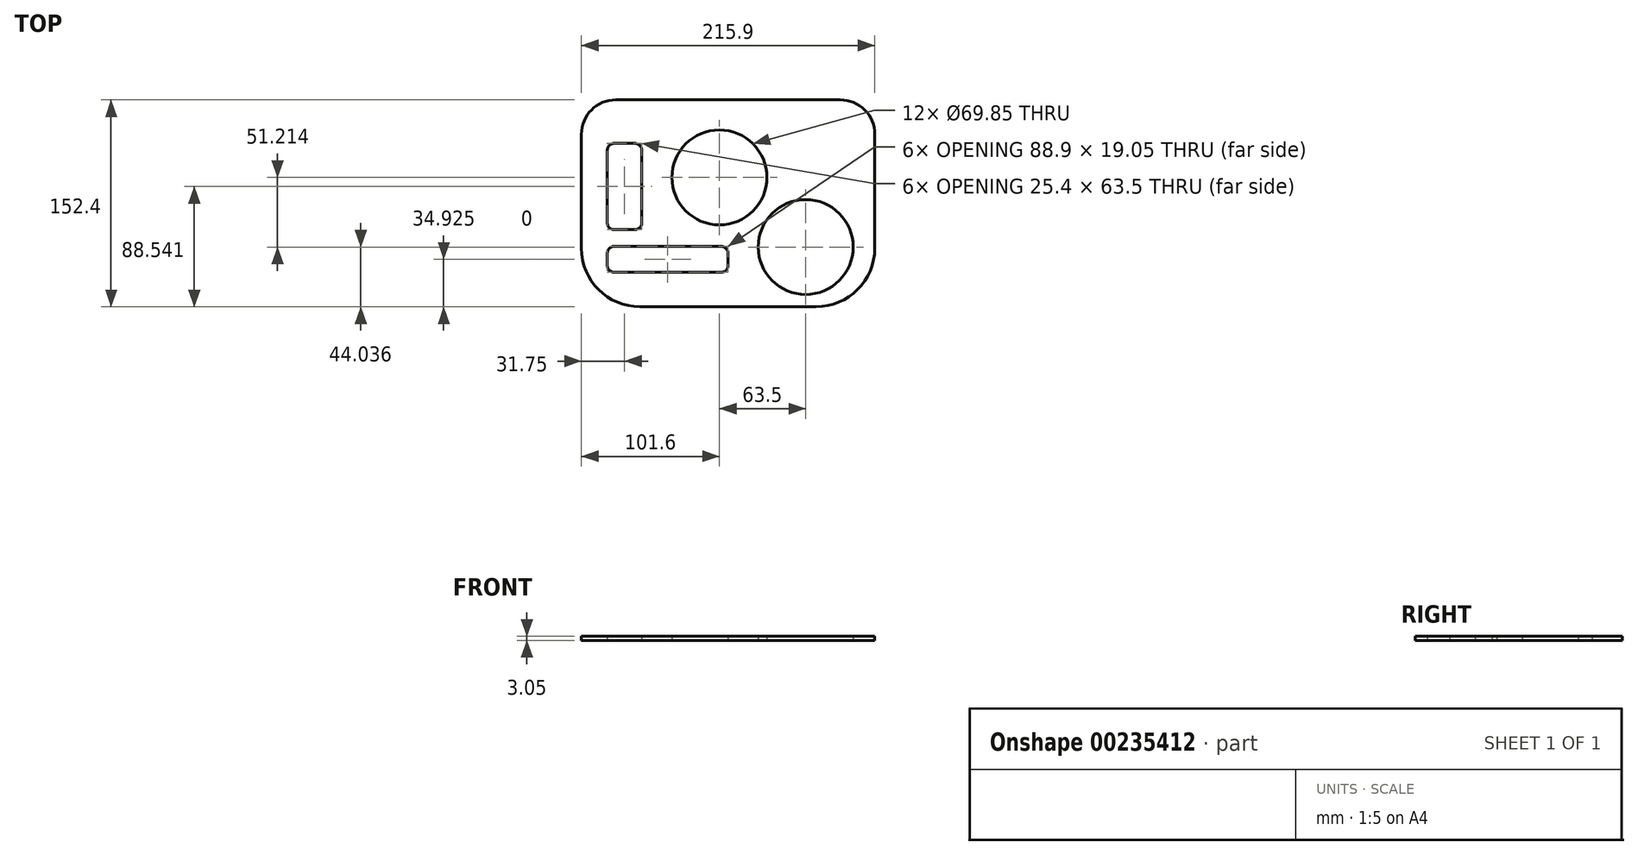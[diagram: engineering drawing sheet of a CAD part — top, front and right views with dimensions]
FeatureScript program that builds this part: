
annotation { "Feature Type Name" : "Feature", "Feature Type Description" : "" }
export const myFeature = defineFeature(function(context is Context, id is Id, definition is map)
    precondition{}
    {
        {
            var Q0;
            Q0=qCreatedBy(makeId("Top.planeOp"),FACE);
            var sketch = newSketch(context, id + "F0", { "sketchPlane" : qUnion([Q0])});
            skLineSegment(sketch, "E0.bottom", {"start": v(107.95, 76.2) * mm, "end": v(-107.95, 76.2) * mm});
            skLineSegment(sketch, "E0.top", {"start": v(107.95, -76.2) * mm, "end": v(-107.95, -76.2) * mm});
            skLineSegment(sketch, "E0.left", {"start": v(107.95, 76.2) * mm, "end": v(107.95, -76.2) * mm});
            skLineSegment(sketch, "E0.right", {"start": v(-107.95, 76.2) * mm, "end": v(-107.95, -76.2) * mm});
            skPoint(sketch, "E0.middle", {"position": v(0, 0) * mm});
            skSolve(sketch);
        }
        {
            var Q0;
            Q0 = qSketchRegion(id + "F0", true);
            extrude(context, id + "F1", {"entities" : qUnion([Q0]), "depth" : 3.05 * mm});
        }
        {
            var Q0;
            Q0=qCreatedBy(makeId("Top.planeOp"),FACE);
            var sketch = newSketch(context, id + "F2", { "sketchPlane" : qUnion([Q0])});
            skLineSegment(sketch, "E1.bottom", {"start": v(-63.5, -19.4) * mm, "end": v(-88.9, -19.4) * mm});
            skLineSegment(sketch, "E1.top", {"start": v(-63.5, 44.1) * mm, "end": v(-88.9, 44.1) * mm});
            skLineSegment(sketch, "E1.left", {"start": v(-63.5, -19.4) * mm, "end": v(-63.5, 44.1) * mm});
            skLineSegment(sketch, "E1.right", {"start": v(-88.9, -19.4) * mm, "end": v(-88.9, 44.1) * mm});
            skPoint(sketch, "E1.middle", {"position": v(-76.2, 12.34) * mm});
            skCircle(sketch, "E2", {"center": v(-6.35, 19.05) * mm, "radius": 34.93 * mm});
            skCircle(sketch, "E3", {"center": v(57.15, -32.16) * mm, "radius": 34.93 * mm});
            skLineSegment(sketch, "E4.bottom", {"start": v(0, -50.8) * mm, "end": v(-88.9, -50.8) * mm});
            skLineSegment(sketch, "E4.top", {"start": v(0, -31.75) * mm, "end": v(-88.9, -31.75) * mm});
            skLineSegment(sketch, "E4.left", {"start": v(0, -50.8) * mm, "end": v(0, -31.75) * mm});
            skLineSegment(sketch, "E4.right", {"start": v(-88.9, -50.8) * mm, "end": v(-88.9, -31.75) * mm});
            skPoint(sketch, "E4.middle", {"position": v(-44.45, -41.27) * mm});
            skSolve(sketch);
        }
        {
            var Q0;
            Q0 = qSketchRegion(id + "F2", true);
            extrude(context, id + "F3", {"entities" : qUnion([Q0]), "operationType" : NewBodyOperationType.REMOVE, "depth" : 25.4 * mm});
        }
        {
            var Q0;
            Q0=makeQuery(id+"F1.opExtrude","SWEPT_EDGE",EDGE,{"disambiguationData":[OSD([sQuery(id+"F0.wireOp",EDGE,"E0.top"),sQuery(id+"F0.wireOp",EDGE,"E0.right")])]});
            var Q1;
            Q1=makeQuery(id+"F1.opExtrude","SWEPT_EDGE",EDGE,{"disambiguationData":[OSD([sQuery(id+"F0.wireOp",EDGE,"E0.top"),sQuery(id+"F0.wireOp",EDGE,"E0.left")])]});
            fillet(context, id + "F4", {"entities" : qUnion([Q0, Q1]), "radius" : 43.18 * mm, "tangentPropagation" : true, "allowEdgeOverflow" : false});
        }
        {
            var Q0;
            Q0=makeQuery(id+"F3.boolean.opBoolean","COPY",EDGE,{"derivedFrom":makeQuery(id+"F3.opExtrude","SWEPT_EDGE",EDGE,{"disambiguationData":[OSD([sQuery(id+"F2.wireOp",EDGE,"E1.top"),sQuery(id+"F2.wireOp",EDGE,"E1.right")])]})});
            var Q1;
            Q1=makeQuery(id+"F3.boolean.opBoolean","COPY",EDGE,{"derivedFrom":makeQuery(id+"F3.opExtrude","SWEPT_EDGE",EDGE,{"disambiguationData":[OSD([sQuery(id+"F2.wireOp",EDGE,"E1.top"),sQuery(id+"F2.wireOp",EDGE,"E1.left")])]})});
            var Q2;
            Q2=makeQuery(id+"F3.boolean.opBoolean","COPY",EDGE,{"derivedFrom":makeQuery(id+"F3.opExtrude","SWEPT_EDGE",EDGE,{"disambiguationData":[OSD([sQuery(id+"F2.wireOp",EDGE,"E1.bottom"),sQuery(id+"F2.wireOp",EDGE,"E1.right")])]})});
            var Q3;
            Q3=makeQuery(id+"F3.boolean.opBoolean","COPY",EDGE,{"derivedFrom":makeQuery(id+"F3.opExtrude","SWEPT_EDGE",EDGE,{"disambiguationData":[OSD([sQuery(id+"F2.wireOp",EDGE,"E1.bottom"),sQuery(id+"F2.wireOp",EDGE,"E1.left")])]})});
            var Q4;
            Q4=makeQuery(id+"F3.boolean.opBoolean","COPY",EDGE,{"derivedFrom":makeQuery(id+"F3.opExtrude","SWEPT_EDGE",EDGE,{"disambiguationData":[OSD([sQuery(id+"F2.wireOp",EDGE,"E4.bottom"),sQuery(id+"F2.wireOp",EDGE,"E4.left")])]})});
            var Q5;
            Q5=makeQuery(id+"F3.boolean.opBoolean","COPY",EDGE,{"derivedFrom":makeQuery(id+"F3.opExtrude","SWEPT_EDGE",EDGE,{"disambiguationData":[OSD([sQuery(id+"F2.wireOp",EDGE,"E4.top"),sQuery(id+"F2.wireOp",EDGE,"E4.left")])]})});
            var Q6;
            Q6=makeQuery(id+"F3.boolean.opBoolean","COPY",EDGE,{"derivedFrom":makeQuery(id+"F3.opExtrude","SWEPT_EDGE",EDGE,{"disambiguationData":[OSD([sQuery(id+"F2.wireOp",EDGE,"E4.bottom"),sQuery(id+"F2.wireOp",EDGE,"E4.right")])]})});
            var Q7;
            Q7=makeQuery(id+"F3.boolean.opBoolean","COPY",EDGE,{"derivedFrom":makeQuery(id+"F3.opExtrude","SWEPT_EDGE",EDGE,{"disambiguationData":[OSD([sQuery(id+"F2.wireOp",EDGE,"E4.top"),sQuery(id+"F2.wireOp",EDGE,"E4.right")])]})});
            fillet(context, id + "F5", {"entities" : qUnion([Q0, Q1, Q2, Q3, Q4, Q5, Q6, Q7]), "radius" : 5.08 * mm, "tangentPropagation" : true, "allowEdgeOverflow" : false});
        }
        {
            var Q0;
            Q0=makeQuery(id+"F1.opExtrude","SWEPT_EDGE",EDGE,{"disambiguationData":[OSD([sQuery(id+"F0.wireOp",EDGE,"E0.bottom"),sQuery(id+"F0.wireOp",EDGE,"E0.right")])]});
            var Q1;
            Q1=makeQuery(id+"F1.opExtrude","SWEPT_EDGE",EDGE,{"disambiguationData":[OSD([sQuery(id+"F0.wireOp",EDGE,"E0.bottom"),sQuery(id+"F0.wireOp",EDGE,"E0.left")])]});
            fillet(context, id + "F6", {"entities" : qUnion([Q0, Q1]), "radius" : 25.4 * mm, "tangentPropagation" : true, "allowEdgeOverflow" : false});
        }
    });
